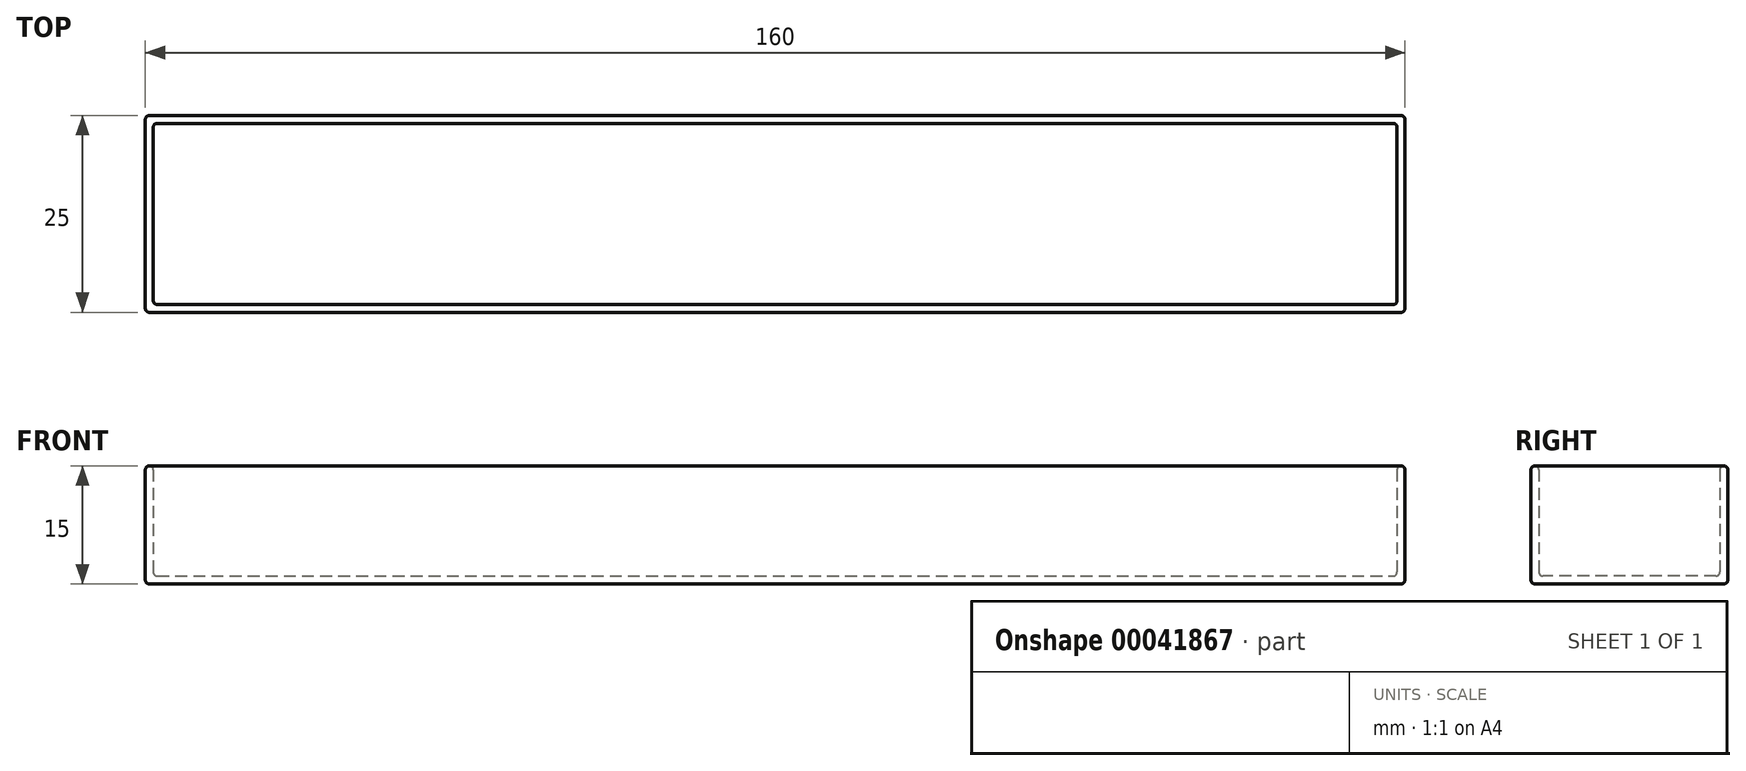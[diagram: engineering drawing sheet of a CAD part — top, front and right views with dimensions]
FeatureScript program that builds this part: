
annotation { "Feature Type Name" : "Feature", "Feature Type Description" : "" }
export const myFeature = defineFeature(function(context is Context, id is Id, definition is map)
    precondition{}
    {
        {
            var Q0;
            Q0=qCreatedBy(makeId("Top.planeOp"),FACE);
            var sketch = newSketch(context, id + "F0", { "sketchPlane" : qUnion([Q0])});
            skLineSegment(sketch, "E0.bottom", {"start": v(-49.13, -25.54) * mm, "end": v(110.87, -25.54) * mm});
            skLineSegment(sketch, "E0.top", {"start": v(-49.13, -50.54) * mm, "end": v(110.87, -50.54) * mm});
            skLineSegment(sketch, "E0.left", {"start": v(-49.13, -25.54) * mm, "end": v(-49.13, -50.54) * mm});
            skLineSegment(sketch, "E0.right", {"start": v(110.87, -25.54) * mm, "end": v(110.87, -50.54) * mm});
            skSolve(sketch);
        }
        {
            var Q0;
            Q0 = qSketchRegion(id + "F0", true);
            extrude(context, id + "F1", {"entities" : qUnion([Q0]), "depth" : 15 * mm});
        }
        {
            var Q0;
            Q0=makeQuery(id+"F1.opExtrude","CAP_FACE",FACE,{"disambiguationData":[OSD([sQuery(id+"F0.wireOp",EDGE,"E0.bottom"),sQuery(id+"F0.wireOp",EDGE,"E0.top"),sQuery(id+"F0.wireOp",EDGE,"E0.left"),sQuery(id+"F0.wireOp",EDGE,"E0.right")])],"isStart":false});
            shell(context, id + "F2", {"entities" : qUnion([Q0]), "thickness" : 1 * mm});
        }
        {
            var Q0;
            Q0=makeQuery(id+"F1.opExtrude","CAP_EDGE",EDGE,{"disambiguationData":[OSD([sQuery(id+"F0.wireOp",EDGE,"E0.bottom")])],"isStart":true});
            var Q1;
            Q1=makeQuery(id+"F1.opExtrude","CAP_EDGE",EDGE,{"disambiguationData":[OSD([sQuery(id+"F0.wireOp",EDGE,"E0.right")])],"isStart":true});
            var Q2;
            Q2=makeQuery(id+"F1.opExtrude","CAP_EDGE",EDGE,{"disambiguationData":[OSD([sQuery(id+"F0.wireOp",EDGE,"E0.left")])],"isStart":true});
            var Q3;
            Q3=makeQuery(id+"F1.opExtrude","CAP_EDGE",EDGE,{"disambiguationData":[OSD([sQuery(id+"F0.wireOp",EDGE,"E0.top")])],"isStart":true});
            var Q4;
            Q4=makeQuery(id+"F1.opExtrude","SWEPT_EDGE",EDGE,{"disambiguationData":[OSD([sQuery(id+"F0.wireOp",EDGE,"E0.bottom"),sQuery(id+"F0.wireOp",EDGE,"E0.right")])]});
            var Q5;
            Q5=makeQuery(id+"F1.opExtrude","SWEPT_EDGE",EDGE,{"disambiguationData":[OSD([sQuery(id+"F0.wireOp",EDGE,"E0.bottom"),sQuery(id+"F0.wireOp",EDGE,"E0.left")])]});
            var Q6;
            Q6=makeQuery(id+"F1.opExtrude","SWEPT_EDGE",EDGE,{"disambiguationData":[OSD([sQuery(id+"F0.wireOp",EDGE,"E0.top"),sQuery(id+"F0.wireOp",EDGE,"E0.left")])]});
            var Q7;
            Q7=makeQuery(id+"F1.opExtrude","SWEPT_EDGE",EDGE,{"disambiguationData":[OSD([sQuery(id+"F0.wireOp",EDGE,"E0.top"),sQuery(id+"F0.wireOp",EDGE,"E0.right")])]});
            fillet(context, id + "F3", {"entities" : qUnion([Q0, Q1, Q2, Q3, Q4, Q5, Q6, Q7]), "radius" : 0.5 * mm, "tangentPropagation" : true, "allowEdgeOverflow" : false});
        }
        {
            var Q0;
            {var subQ0=sQuery(id+"F0.wireOp",EDGE,"E0.left");Q0=makeQuery(id+"F2.opShell","OFFSET_EDGE",EDGE,{"disambiguationData":[OSD([subQ0]),TDD([makeQuery(id+"F1.opExtrude","CAP_EDGE",EDGE,{"disambiguationData":[OSD([subQ0])],"isStart":true})])]});}
            var Q1;
            {var subQ0=sQuery(id+"F0.wireOp",EDGE,"E0.bottom");Q1=makeQuery(id+"F2.opShell","OFFSET_EDGE",EDGE,{"disambiguationData":[OSD([subQ0]),TDD([makeQuery(id+"F1.opExtrude","CAP_EDGE",EDGE,{"disambiguationData":[OSD([subQ0])],"isStart":true})])]});}
            var Q2;
            {var subQ0=sQuery(id+"F0.wireOp",EDGE,"E0.top");Q2=makeQuery(id+"F2.opShell","OFFSET_EDGE",EDGE,{"disambiguationData":[OSD([subQ0]),TDD([makeQuery(id+"F1.opExtrude","CAP_EDGE",EDGE,{"disambiguationData":[OSD([subQ0])],"isStart":true})])]});}
            var Q3;
            {var subQ0=sQuery(id+"F0.wireOp",EDGE,"E0.right");Q3=makeQuery(id+"F2.opShell","OFFSET_EDGE",EDGE,{"disambiguationData":[OSD([subQ0]),TDD([makeQuery(id+"F1.opExtrude","CAP_EDGE",EDGE,{"disambiguationData":[OSD([subQ0])],"isStart":true})])]});}
            var Q4;
            Q4=makeQuery(id+"F2.opShell","OFFSET_EDGE",EDGE,{"disambiguationData":[OSD([sQuery(id+"F0.wireOp",EDGE,"E0.bottom"),sQuery(id+"F0.wireOp",EDGE,"E0.left")])]});
            var Q5;
            Q5=makeQuery(id+"F2.opShell","OFFSET_EDGE",EDGE,{"disambiguationData":[OSD([sQuery(id+"F0.wireOp",EDGE,"E0.top"),sQuery(id+"F0.wireOp",EDGE,"E0.left")])]});
            var Q6;
            Q6=makeQuery(id+"F2.opShell","OFFSET_EDGE",EDGE,{"disambiguationData":[OSD([sQuery(id+"F0.wireOp",EDGE,"E0.bottom"),sQuery(id+"F0.wireOp",EDGE,"E0.right")])]});
            var Q7;
            Q7=makeQuery(id+"F2.opShell","OFFSET_EDGE",EDGE,{"disambiguationData":[OSD([sQuery(id+"F0.wireOp",EDGE,"E0.top"),sQuery(id+"F0.wireOp",EDGE,"E0.right")])]});
            fillet(context, id + "F4", {"entities" : qUnion([Q0, Q1, Q2, Q3, Q4, Q5, Q6, Q7]), "radius" : 0.5 * mm, "tangentPropagation" : true, "allowEdgeOverflow" : false});
        }
        {
            var Q0;
            Q0=makeQuery(id+"F1.opExtrude","CAP_EDGE",EDGE,{"disambiguationData":[OSD([sQuery(id+"F0.wireOp",EDGE,"E0.bottom")])],"isStart":false});
            var Q1;
            {var subQ0=sQuery(id+"F0.wireOp",EDGE,"E0.bottom");Q1=makeQuery(id+"F2.opShell","OFFSET_EDGE",EDGE,{"disambiguationData":[OSD([subQ0]),TDD([makeQuery(id+"F1.opExtrude","CAP_EDGE",EDGE,{"disambiguationData":[OSD([subQ0])],"isStart":false})])]});}
            var Q2;
            {var subQ0=sQuery(id+"F0.wireOp",EDGE,"E0.top");Q2=makeQuery(id+"F2.opShell","OFFSET_EDGE",EDGE,{"disambiguationData":[OSD([subQ0]),TDD([makeQuery(id+"F1.opExtrude","CAP_EDGE",EDGE,{"disambiguationData":[OSD([subQ0])],"isStart":false})])]});}
            var Q3;
            Q3=makeQuery(id+"F1.opExtrude","CAP_EDGE",EDGE,{"disambiguationData":[OSD([sQuery(id+"F0.wireOp",EDGE,"E0.top")])],"isStart":false});
            var Q4;
            {var subQ0=sQuery(id+"F0.wireOp",EDGE,"E0.right");Q4=makeQuery(id+"F2.opShell","OFFSET_EDGE",EDGE,{"disambiguationData":[OSD([subQ0]),TDD([makeQuery(id+"F1.opExtrude","CAP_EDGE",EDGE,{"disambiguationData":[OSD([subQ0])],"isStart":false})])]});}
            var Q5;
            Q5=makeQuery(id+"F1.opExtrude","CAP_EDGE",EDGE,{"disambiguationData":[OSD([sQuery(id+"F0.wireOp",EDGE,"E0.right")])],"isStart":false});
            var Q6;
            Q6=makeQuery(id+"F1.opExtrude","CAP_EDGE",EDGE,{"disambiguationData":[OSD([sQuery(id+"F0.wireOp",EDGE,"E0.left")])],"isStart":false});
            var Q7;
            {var subQ0=sQuery(id+"F0.wireOp",EDGE,"E0.left");Q7=makeQuery(id+"F2.opShell","OFFSET_EDGE",EDGE,{"disambiguationData":[OSD([subQ0]),TDD([makeQuery(id+"F1.opExtrude","CAP_EDGE",EDGE,{"disambiguationData":[OSD([subQ0])],"isStart":false})])]});}
            var Q8;
            {var subQ0=sQuery(id+"F0.wireOp",EDGE,"E0.top");var subQ1=sQuery(id+"F0.wireOp",EDGE,"E0.left");Q8=makeQuery(id+"F4.opFillet","BLEND_EDGE",EDGE,{"blendedFrom":[makeQuery(id+"F2.opShell","OFFSET_EDGE",EDGE,{"disambiguationData":[OSD([subQ0,subQ1])]}),makeQuery(id+"F1.opExtrude","CAP_FACE",FACE,{"disambiguationData":[OSD([sQuery(id+"F0.wireOp",EDGE,"E0.bottom"),subQ0,subQ1,sQuery(id+"F0.wireOp",EDGE,"E0.right")])],"isStart":false})],"blendedInto":[makeQuery(id+"F1.opExtrude","CAP_FACE",FACE,{"disambiguationData":[OSD([sQuery(id+"F0.wireOp",EDGE,"E0.bottom"),subQ0,subQ1,sQuery(id+"F0.wireOp",EDGE,"E0.right")])],"isStart":false})]});}
            var Q9;
            {var subQ0=sQuery(id+"F0.wireOp",EDGE,"E0.bottom");var subQ1=sQuery(id+"F0.wireOp",EDGE,"E0.left");Q9=makeQuery(id+"F4.opFillet","BLEND_EDGE",EDGE,{"blendedFrom":[makeQuery(id+"F2.opShell","OFFSET_EDGE",EDGE,{"disambiguationData":[OSD([subQ0,subQ1])]}),makeQuery(id+"F1.opExtrude","CAP_FACE",FACE,{"disambiguationData":[OSD([subQ0,sQuery(id+"F0.wireOp",EDGE,"E0.top"),subQ1,sQuery(id+"F0.wireOp",EDGE,"E0.right")])],"isStart":false})],"blendedInto":[makeQuery(id+"F1.opExtrude","CAP_FACE",FACE,{"disambiguationData":[OSD([subQ0,sQuery(id+"F0.wireOp",EDGE,"E0.top"),subQ1,sQuery(id+"F0.wireOp",EDGE,"E0.right")])],"isStart":false})]});}
            var Q10;
            {var subQ0=sQuery(id+"F0.wireOp",EDGE,"E0.bottom");var subQ1=sQuery(id+"F0.wireOp",EDGE,"E0.left");Q10=makeQuery(id+"F3.opFillet","BLEND_EDGE",EDGE,{"blendedFrom":[makeQuery(id+"F1.opExtrude","SWEPT_EDGE",EDGE,{"disambiguationData":[OSD([subQ0,subQ1])]}),makeQuery(id+"F1.opExtrude","CAP_FACE",FACE,{"disambiguationData":[OSD([subQ0,sQuery(id+"F0.wireOp",EDGE,"E0.top"),subQ1,sQuery(id+"F0.wireOp",EDGE,"E0.right")])],"isStart":false})],"blendedInto":[makeQuery(id+"F1.opExtrude","CAP_FACE",FACE,{"disambiguationData":[OSD([subQ0,sQuery(id+"F0.wireOp",EDGE,"E0.top"),subQ1,sQuery(id+"F0.wireOp",EDGE,"E0.right")])],"isStart":false})]});}
            var Q11;
            {var subQ0=sQuery(id+"F0.wireOp",EDGE,"E0.top");var subQ1=sQuery(id+"F0.wireOp",EDGE,"E0.left");Q11=makeQuery(id+"F3.opFillet","BLEND_EDGE",EDGE,{"blendedFrom":[makeQuery(id+"F1.opExtrude","SWEPT_EDGE",EDGE,{"disambiguationData":[OSD([subQ0,subQ1])]}),makeQuery(id+"F1.opExtrude","CAP_FACE",FACE,{"disambiguationData":[OSD([sQuery(id+"F0.wireOp",EDGE,"E0.bottom"),subQ0,subQ1,sQuery(id+"F0.wireOp",EDGE,"E0.right")])],"isStart":false})],"blendedInto":[makeQuery(id+"F1.opExtrude","CAP_FACE",FACE,{"disambiguationData":[OSD([sQuery(id+"F0.wireOp",EDGE,"E0.bottom"),subQ0,subQ1,sQuery(id+"F0.wireOp",EDGE,"E0.right")])],"isStart":false})]});}
            var Q12;
            {var subQ0=sQuery(id+"F0.wireOp",EDGE,"E0.bottom");var subQ1=sQuery(id+"F0.wireOp",EDGE,"E0.right");Q12=makeQuery(id+"F4.opFillet","BLEND_EDGE",EDGE,{"blendedFrom":[makeQuery(id+"F2.opShell","OFFSET_EDGE",EDGE,{"disambiguationData":[OSD([subQ0,subQ1])]}),makeQuery(id+"F1.opExtrude","CAP_FACE",FACE,{"disambiguationData":[OSD([subQ0,sQuery(id+"F0.wireOp",EDGE,"E0.top"),sQuery(id+"F0.wireOp",EDGE,"E0.left"),subQ1])],"isStart":false})],"blendedInto":[makeQuery(id+"F1.opExtrude","CAP_FACE",FACE,{"disambiguationData":[OSD([subQ0,sQuery(id+"F0.wireOp",EDGE,"E0.top"),sQuery(id+"F0.wireOp",EDGE,"E0.left"),subQ1])],"isStart":false})]});}
            var Q13;
            {var subQ0=sQuery(id+"F0.wireOp",EDGE,"E0.bottom");var subQ1=sQuery(id+"F0.wireOp",EDGE,"E0.right");Q13=makeQuery(id+"F3.opFillet","BLEND_EDGE",EDGE,{"blendedFrom":[makeQuery(id+"F1.opExtrude","SWEPT_EDGE",EDGE,{"disambiguationData":[OSD([subQ0,subQ1])]}),makeQuery(id+"F1.opExtrude","CAP_FACE",FACE,{"disambiguationData":[OSD([subQ0,sQuery(id+"F0.wireOp",EDGE,"E0.top"),sQuery(id+"F0.wireOp",EDGE,"E0.left"),subQ1])],"isStart":false})],"blendedInto":[makeQuery(id+"F1.opExtrude","CAP_FACE",FACE,{"disambiguationData":[OSD([subQ0,sQuery(id+"F0.wireOp",EDGE,"E0.top"),sQuery(id+"F0.wireOp",EDGE,"E0.left"),subQ1])],"isStart":false})]});}
            var Q14;
            {var subQ0=sQuery(id+"F0.wireOp",EDGE,"E0.top");var subQ1=sQuery(id+"F0.wireOp",EDGE,"E0.right");Q14=makeQuery(id+"F4.opFillet","BLEND_EDGE",EDGE,{"blendedFrom":[makeQuery(id+"F2.opShell","OFFSET_EDGE",EDGE,{"disambiguationData":[OSD([subQ0,subQ1])]}),makeQuery(id+"F1.opExtrude","CAP_FACE",FACE,{"disambiguationData":[OSD([sQuery(id+"F0.wireOp",EDGE,"E0.bottom"),subQ0,sQuery(id+"F0.wireOp",EDGE,"E0.left"),subQ1])],"isStart":false})],"blendedInto":[makeQuery(id+"F1.opExtrude","CAP_FACE",FACE,{"disambiguationData":[OSD([sQuery(id+"F0.wireOp",EDGE,"E0.bottom"),subQ0,sQuery(id+"F0.wireOp",EDGE,"E0.left"),subQ1])],"isStart":false})]});}
            var Q15;
            {var subQ0=sQuery(id+"F0.wireOp",EDGE,"E0.top");var subQ1=sQuery(id+"F0.wireOp",EDGE,"E0.right");Q15=makeQuery(id+"F3.opFillet","BLEND_EDGE",EDGE,{"blendedFrom":[makeQuery(id+"F1.opExtrude","SWEPT_EDGE",EDGE,{"disambiguationData":[OSD([subQ0,subQ1])]}),makeQuery(id+"F1.opExtrude","CAP_FACE",FACE,{"disambiguationData":[OSD([sQuery(id+"F0.wireOp",EDGE,"E0.bottom"),subQ0,sQuery(id+"F0.wireOp",EDGE,"E0.left"),subQ1])],"isStart":false})],"blendedInto":[makeQuery(id+"F1.opExtrude","CAP_FACE",FACE,{"disambiguationData":[OSD([sQuery(id+"F0.wireOp",EDGE,"E0.bottom"),subQ0,sQuery(id+"F0.wireOp",EDGE,"E0.left"),subQ1])],"isStart":false})]});}
            fillet(context, id + "F5", {"entities" : qUnion([Q0, Q1, Q2, Q3, Q4, Q5, Q6, Q7, Q8, Q9, Q10, Q11, Q12, Q13, Q14, Q15]), "radius" : 0.5 * mm, "tangentPropagation" : true, "allowEdgeOverflow" : false});
        }
    });
